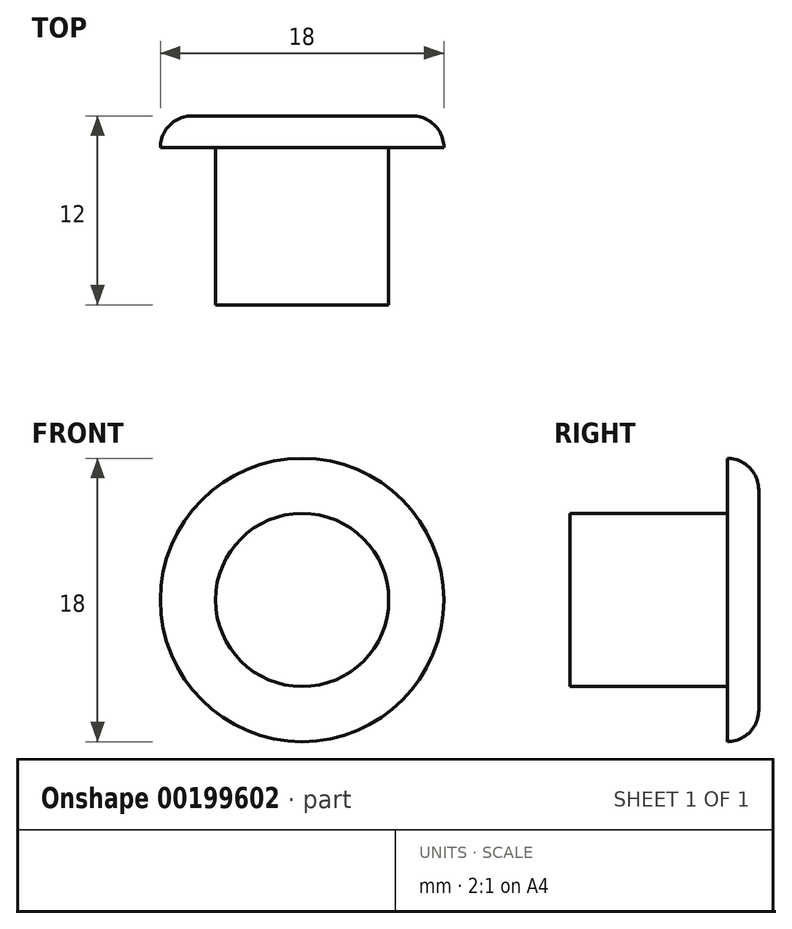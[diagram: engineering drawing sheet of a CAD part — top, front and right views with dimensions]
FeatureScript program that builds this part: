
annotation { "Feature Type Name" : "Feature", "Feature Type Description" : "" }
export const myFeature = defineFeature(function(context is Context, id is Id, definition is map)
    precondition{}
    {
        {
            var Q0;
            Q0=qCreatedBy(makeId("Front.planeOp"),FACE);
            var sketch = newSketch(context, id + "F0", { "sketchPlane" : qUnion([Q0])});
            skCircle(sketch, "E0", {"center": v(0, 0) * mm, "radius": 9 * mm});
            skSolve(sketch);
        }
        {
            var Q0;
            Q0 = qSketchRegion(id + "F0", true);
            extrude(context, id + "F1", {"entities" : qUnion([Q0]), "depth" : 12 * mm});
        }
        {
            var Q0;
            Q0=makeQuery(id+"F1.opExtrude","CAP_FACE",FACE,{"disambiguationData":[OSD([sQuery(id+"F0.wireOp",EDGE,"E0")])],"isStart":false});
            var sketch = newSketch(context, id + "F2", { "sketchPlane" : qUnion([Q0])});
            skCircle(sketch, "E1", {"center": v(0, 0) * mm, "radius": 5.5 * mm});
            skSolve(sketch);
        }
        {
            var Q0;
            Q0=makeQuery(id+"F1.opExtrude","CAP_FACE",FACE,{"disambiguationData":[OSD([sQuery(id+"F0.wireOp",EDGE,"E0")])],"isStart":true});
            fillet(context, id + "F3", {"entities" : qUnion([Q0]), "radius" : 2 * mm, "tangentPropagation" : true, "allowEdgeOverflow" : false});
        }
        {
            var Q0;
            Q0=makeQuery(id+"F2.imprint","IMPRINT",FACE,{"disambiguationData":[TD([[makeQuery(id+"F2.imprint","IMPRINT",EDGE,{"derivedFrom":sQuery(id+"F2.wireOp",EDGE,"E1")}),-1.0]])]});
            extrude(context, id + "F4", {"entities" : qUnion([Q0]), "operationType" : NewBodyOperationType.REMOVE, "oppositeDirection" : true, "depth" : 10 * mm});
        }
    });
